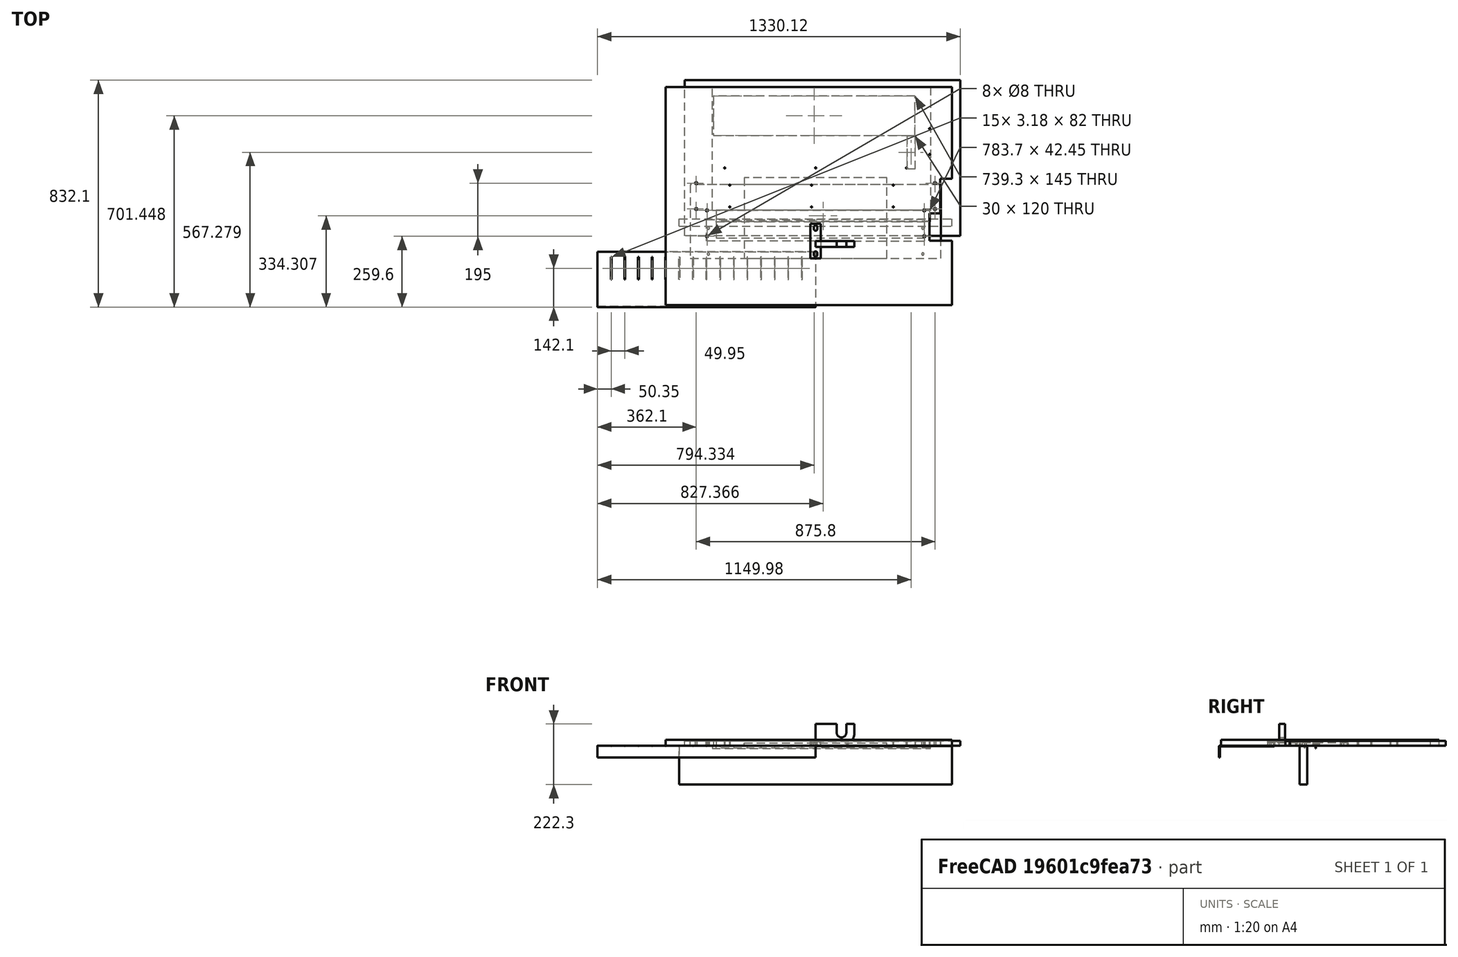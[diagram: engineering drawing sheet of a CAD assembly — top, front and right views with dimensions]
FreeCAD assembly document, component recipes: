
FREECAD ASSEMBLY — COMPONENT RECIPES ("cutting3")

This assembly document has 11 components, labeled P0..P10 below (a component is one placed body or linked part). 11 of them carry a construction recipe — the FreeCAD feature program that regenerates the part from scratch, quoted from this document or its linked companion documents; the rest are supplied as boundary geometry only. No exploded tour is included for this assembly.
COMPONENT P0 — recipe-attached ("filler_21", modeled in this document).
Construction recipe (the document's own serialized feature program — sketch geometry with constraints, then the solid features built on it; lengths are millimeters unless a unit is written):

FEATURE [Sketcher::SketchObject] Sketch006
  AttachmentSupport = -> [XY_Plane006]
  FullyConstrained = false
  MapMode = 5
  sketch-geometry (9):
    g0: LineSegment StartX=0 StartY=0 StartZ=0 EndX=19 EndY=0 EndZ=0
    g1: LineSegment StartX=19 StartY=0 StartZ=0 EndX=19 EndY=63.5 EndZ=0
    g2: LineSegment StartX=19 StartY=63.5 StartZ=0 EndX=0 EndY=63.5 EndZ=0
    g3: LineSegment StartX=0 StartY=63.5 StartZ=0 EndX=0 EndY=57 EndZ=0
    g4: ArcOfCircle CenterX=0 CenterY=44.5 CenterZ=0 NormalX=0 NormalY=0 NormalZ=1 AngleXU=0 Radius=6.5 StartAngle=4.7122 EndAngle=6.28319
    g5: ArcOfCircle CenterX=0 CenterY=50.5 CenterZ=0 NormalX=0 NormalY=0 NormalZ=1 AngleXU=0 Radius=6.5 StartAngle=3.65e-14 EndAngle=1.5708
    g6: LineSegment StartX=6.5 StartY=44.5 StartZ=0 EndX=6.5 EndY=50.5 EndZ=0
    g7: LineSegment StartX=-0.00123483 StartY=38 StartZ=0 EndX=0 EndY=0 EndZ=0
    g8: GeomPoint X=0 Y=47.5 Z=0
  constraints (23):
    c: Coincident(g0,g1)
    c: Coincident(g1,g2)
    c: Coincident(g2,g3)
    c: Coincident(g7,g0)
    c: Horizontal(g0)
    c: Horizontal(g2)
    c: Vertical(g1)
    c: Vertical(g3)
    c: Coincident(g0,g-1)
    c: DistanceX(g1) = 19
    c: DistanceY(g1) = 63.5
    c: Tangent(g4,g6) = -1.5708
    c: Tangent(g6,g5) = -1.5708
    c: Equal(g4,g5)
    c: PointOnObject(g4,g3)
    c: PointOnObject(g5,g3)
    c: Coincident(g3,g5)
    c: Coincident(g7,g4)
    c: DistanceY(g4,g3) = 19
    c: Diameter(g4) = 13
    c: PointOnObject(g8,g-2)
    c: Symmetric(g4,g5,g8)
    c: DistanceY(g8) = 47.5
FEATURE [PartDesign::Pad] Pad006
  Direction = (0,0,1)
  Length = 21
  Length2 = 10
  Profile = -> Sketch006
  ReferenceAxis = -> Sketch006 [N_Axis]
  Suppressed = false
  Type = 0
FEATURE [PartDesign::Mirrored] Mirrored002
  MirrorPlane = -> Sketch006 [V_Axis]
  Suppressed = false
FEATURE [PartDesign::Mirrored] Mirrored003
  MirrorPlane = -> Sketch006 [H_Axis]
  Suppressed = false
FEATURE [PartDesign::MultiTransform] MultiTransform
  BaseFeature = -> Pad006
  Originals = -> [Pad006]
  Suppressed = false
  Transformations = -> [Mirrored002,Mirrored003]
FEATURE [PartDesign::Body] Body002  label="filler_21"
  Group = -> [Sketch006,Pad006,MultiTransform,Mirrored002,Mirrored003]
  Origin = -> Origin006
  Tip = -> MultiTransform
COMPONENT P1 — recipe-attached ("filler_14.6", modeled in this document).
Construction recipe (the document's own serialized feature program — sketch geometry with constraints, then the solid features built on it; lengths are millimeters unless a unit is written):

FEATURE [Sketcher::SketchObject] Sketch007
  AttachmentSupport = -> [XY_Plane008]
  FullyConstrained = false
  MapMode = 5
  sketch-geometry (9):
    g0: LineSegment StartX=0 StartY=0 StartZ=0 EndX=19 EndY=0 EndZ=0
    g1: LineSegment StartX=19 StartY=0 StartZ=0 EndX=19 EndY=63.5 EndZ=0
    g2: LineSegment StartX=19 StartY=63.5 StartZ=0 EndX=0 EndY=63.5 EndZ=0
    g3: LineSegment StartX=0 StartY=63.5 StartZ=0 EndX=0 EndY=57 EndZ=0
    g4: ArcOfCircle CenterX=0 CenterY=44.5 CenterZ=0 NormalX=0 NormalY=0 NormalZ=1 AngleXU=0 Radius=6.5 StartAngle=4.7122 EndAngle=6.28319
    g5: ArcOfCircle CenterX=0 CenterY=50.5 CenterZ=0 NormalX=0 NormalY=0 NormalZ=1 AngleXU=0 Radius=6.5 StartAngle=3.65e-14 EndAngle=1.5708
    g6: LineSegment StartX=6.5 StartY=44.5 StartZ=0 EndX=6.5 EndY=50.5 EndZ=0
    g7: LineSegment StartX=-0.00123483 StartY=38 StartZ=0 EndX=0 EndY=0 EndZ=0
    g8: GeomPoint X=0 Y=47.5 Z=0
  constraints (23):
    c: Coincident(g0,g1)
    c: Coincident(g1,g2)
    c: Coincident(g2,g3)
    c: Coincident(g7,g0)
    c: Horizontal(g0)
    c: Horizontal(g2)
    c: Vertical(g1)
    c: Vertical(g3)
    c: Coincident(g0,g-1)
    c: DistanceX(g1) = 19
    c: DistanceY(g1) = 63.5
    c: Tangent(g4,g6) = -1.5708
    c: Tangent(g6,g5) = -1.5708
    c: Equal(g4,g5)
    c: PointOnObject(g4,g3)
    c: PointOnObject(g5,g3)
    c: Coincident(g3,g5)
    c: Coincident(g7,g4)
    c: DistanceY(g4,g3) = 19
    c: Diameter(g4) = 13
    c: PointOnObject(g8,g-2)
    c: Symmetric(g4,g5,g8)
    c: DistanceY(g8) = 47.5
FEATURE [PartDesign::Mirrored] Mirrored004
  MirrorPlane = -> Sketch007 [V_Axis]
  Suppressed = false
FEATURE [PartDesign::Mirrored] Mirrored005
  MirrorPlane = -> Sketch007 [H_Axis]
  Suppressed = false
FEATURE [PartDesign::Pad] Pad007
  Direction = (0,0,1)
  Length = 14.6
  Length2 = 10
  Profile = -> Sketch007
  ReferenceAxis = -> Sketch007 [N_Axis]
  Suppressed = false
  Type = 0
FEATURE [PartDesign::MultiTransform] MultiTransform001
  BaseFeature = -> Pad007
  Originals = -> [Pad007]
  Suppressed = false
  Transformations = -> [Mirrored004,Mirrored005]
FEATURE [PartDesign::Body] Body004  label="filler_14.6"
  Group = -> [Sketch007,Pad007,MultiTransform001,Mirrored004,Mirrored005]
  Origin = -> Origin008
  Tip = -> MultiTransform001
COMPONENT P2 — recipe-attached ("table1_ss", modeled in this document).
Construction recipe (the document's own serialized feature program — sketch geometry with constraints, then the solid features built on it; lengths are millimeters unless a unit is written):

FEATURE [PartDesign::SubShapeBinder] Binder002
  BindCopyOnChange = 0
  BindMode = 0
  ClaimChildren = false
  Context = -> Body009 [Binder002.]
  Fuse = false
  MakeFace = true
  OffsetFill = false
  OffsetIntersection = false
  OffsetJoinType = 0
  OffsetOpenResult = false
  PartialLoad = false
  Relative = true
  Support = -> [Body010[Sketch016.]]
  _Version = 2
FEATURE [Sketcher::SketchObject] Sketch010
  AttachmentSupport = -> [XY_Plane010]
  ExternalGeometry = -> [Binder002]
  FullyConstrained = false
  MapMode = 5
  sketch-geometry (4):
    g0: LineSegment StartX=-378.908 StartY=113.432 StartZ=0 EndX=-378.908 EndY=565.012 EndZ=0
    g1: LineSegment StartX=-378.908 StartY=565.012 StartZ=0 EndX=421.092 EndY=565.012 EndZ=0
    g2: LineSegment StartX=421.092 StartY=565.012 StartZ=0 EndX=421.092 EndY=113.432 EndZ=0
    g3: LineSegment StartX=421.092 StartY=113.432 StartZ=0 EndX=-378.908 EndY=113.432 EndZ=0
  constraints (10):
    c: Coincident(g0,g1)
    c: Coincident(g1,g2)
    c: Horizontal(g1)
    c: Vertical(g0)
    c: Vertical(g2)
    c: Coincident(g3,g2)
    c: PointOnObject(g2,g-3)
    c: Coincident(g3,g0)
    c: PointOnObject(g0,g-3)
    c: DistanceX(g3,g3) = 800
FEATURE [PartDesign::FeaturePython] BaseBend001  # WARN: FeaturePython — macro-defined, semantics opaque (R4)
  BendSide = 0
  BendSketch = -> Sketch010
  MidPlane = false
  Reverse = false
  Suppressed = false
  length = 100
  radius = 1
  thickness = 1
FEATURE [PartDesign::FeaturePython] Bend001  # WARN: FeaturePython — macro-defined, semantics opaque (R4)
  AutoMiter = true
  BaseFeature = -> BaseBend001
  BendType = 2
  LengthList = [10]
  LengthSpec = 0
  ReliefFactor = 0.7
  Suppressed = false
  UseReliefFactor = false
  angle = 90
  baseObject = -> BaseBend001 [Edge12]
  bendAList = [90]
  extend1 = 0
  extend2 = 0
  gap1 = 0
  gap2 = 0
  invert = false
  kfactor = 0.5
  length = 10
  maxExtendDist = 5
  minGap = 0.1
  minReliefGap = 1
  miterangle1 = 0
  miterangle2 = 0
  offset = 0
  radius = 1
  reliefType = 0
  reliefd = 1
  reliefw = 0.8
  sketchflip = false
  sketchinvert = false
  unfold = false
  expr: radius = BaseBend001.radius
FEATURE [PartDesign::SubShapeBinder] Binder
  BindCopyOnChange = 0
  BindMode = 0
  ClaimChildren = true
  Context = -> Body009 [Binder.]
  Fuse = false
  MakeFace = true
  OffsetFill = false
  OffsetIntersection = false
  OffsetJoinType = 0
  OffsetOpenResult = false
  PartialLoad = false
  Placement = pos=(-337,460,0) rot=(0,0,1;0rad)
  Relative = true
  Support = -> [Populate]
  _Version = 2
FEATURE [PartDesign::Body] Body009  label="table1_ss"
  Group = -> [Sketch010,Binder,BaseBend001,Binder002,Bend001]
  Origin = -> Origin010
  Tip = -> Bend001
COMPONENT P3 — recipe-attached ("table_plywood", modeled in this document).
Construction recipe (the document's own serialized feature program — sketch geometry with constraints, then the solid features built on it; lengths are millimeters unless a unit is written):

FEATURE [Sketcher::SketchObject] Sketch012
  AttachmentSupport = -> [XY_Plane011]
  FullyConstrained = false
  MapMode = 5
  sketch-geometry (4):
    g0: LineSegment StartX=-479.883 StartY=590 StartZ=0 EndX=530.117 EndY=590 EndZ=0
    g1: LineSegment StartX=530.117 StartY=590 StartZ=0 EndX=530.117 EndY=18.4008 EndZ=0
    g2: LineSegment StartX=530.117 StartY=18.4008 StartZ=0 EndX=-479.883 EndY=18.4008 EndZ=0
    g3: LineSegment StartX=-479.883 StartY=18.4008 StartZ=0 EndX=-479.883 EndY=590 EndZ=0
  constraints (10):
    c: Coincident(g0,g1)
    c: Coincident(g1,g2)
    c: Coincident(g2,g3)
    c: Coincident(g3,g0)
    c: Horizontal(g0)
    c: Horizontal(g2)
    c: Vertical(g1)
    c: Vertical(g3)
    c: DistanceX(g2,g2) = 1010
    c: DistanceY(g0) = 590
FEATURE [Sketcher::SketchObject] Sketch013
  AttachmentSupport = -> [XY_Plane011]
  FullyConstrained = false
  MapMode = 5
  expr: Constraints[8] = Sketch011.Constraints.width + LinearArray.SpanEnd
  expr: Constraints[9] = Sketch011.Constraints.length
  sketch-geometry (4):
    g0: LineSegment StartX=-375.316 StartY=386.848 StartZ=0 EndX=363.984 EndY=386.848 EndZ=0
    g1: LineSegment StartX=363.984 StartY=386.848 StartZ=0 EndX=363.984 EndY=531.848 EndZ=0
    g2: LineSegment StartX=363.984 StartY=531.848 StartZ=0 EndX=-375.316 EndY=531.848 EndZ=0
    g3: LineSegment StartX=-375.316 StartY=531.848 StartZ=0 EndX=-375.316 EndY=386.848 EndZ=0
  constraints (10):
    c: Coincident(g0,g1)
    c: Coincident(g1,g2)
    c: Coincident(g2,g3)
    c: Coincident(g3,g0)
    c: Horizontal(g0)
    c: Horizontal(g2)
    c: Vertical(g1)
    c: Vertical(g3)
    c: DistanceX(g2,g2) = 739.3
    c: DistanceY(g1,g1) = 145
FEATURE [Sketcher::SketchObject] Sketch014
  AttachmentSupport = -> [XY_Plane011]
  FullyConstrained = false
  MapMode = 5
  sketch-geometry (4):
    g0: LineSegment StartX=334.976 StartY=265.179 StartZ=0 EndX=364.976 EndY=265.179 EndZ=0
    g1: LineSegment StartX=364.976 StartY=265.179 StartZ=0 EndX=364.976 EndY=385.179 EndZ=0
    g2: LineSegment StartX=364.976 StartY=385.179 StartZ=0 EndX=334.976 EndY=385.179 EndZ=0
    g3: LineSegment StartX=334.976 StartY=385.179 StartZ=0 EndX=334.976 EndY=265.179 EndZ=0
  constraints (10):
    c: Coincident(g0,g1)
    c: Coincident(g1,g2)
    c: Coincident(g2,g3)
    c: Coincident(g3,g0)
    c: Horizontal(g0)
    c: Horizontal(g2)
    c: Vertical(g1)
    c: Vertical(g3)
    c: DistanceY(g3,g3) = 120
    c: DistanceX(g0,g0) = 30
FEATURE [Sketcher::SketchObject] Sketch016
  AttachmentSupport = -> [XY_Plane011]
  FullyConstrained = false
  MapMode = 5
  sketch-geometry (4):
    g0: LineSegment StartX=-364.484 StartY=70.9815 StartZ=0 EndX=419.215 EndY=70.9815 EndZ=0
    g1: LineSegment StartX=419.215 StartY=70.9815 StartZ=0 EndX=419.215 EndY=113.432 EndZ=0
    g2: LineSegment StartX=419.215 StartY=113.432 StartZ=0 EndX=-364.484 EndY=113.432 EndZ=0
    g3: LineSegment StartX=-364.484 StartY=113.432 StartZ=0 EndX=-364.484 EndY=70.9815 EndZ=0
  constraints (8):
    c: Coincident(g0,g1)
    c: Coincident(g1,g2)
    c: Coincident(g2,g3)
    c: Coincident(g3,g0)
    c: Horizontal(g0)
    c: Horizontal(g2)
    c: Vertical(g1)
    c: Vertical(g3)
FEATURE [PartDesign::Pad] Pad009
  Direction = (0,0,1)
  Length = 18
  Length2 = 10
  Profile = -> Sketch012
  ReferenceAxis = -> Sketch012 [N_Axis]
  Suppressed = false
  Type = 0
FEATURE [PartDesign::SubShapeBinder] Binder003
  BindCopyOnChange = 0
  BindMode = 0
  ClaimChildren = true
  Context = -> Body010 [Binder003.]
  Fuse = false
  MakeFace = true
  OffsetFill = false
  OffsetIntersection = false
  OffsetJoinType = 0
  OffsetOpenResult = false
  PartialLoad = false
  Relative = true
  Support = -> [Sketch014,Sketch013,Sketch016]
  _Version = 2
FEATURE [PartDesign::Pocket] Pocket002
  BaseFeature = -> Pad009
  Direction = (0,0,-1)
  Length = 5
  Length2 = 5
  Midplane = true
  Profile = -> Binder003
  Suppressed = false
  Type = 1
FEATURE [PartDesign::Body] Body010  label="table_plywood"
  Group = -> [Sketch012,Sketch013,Sketch014,Sketch016,Pad009,Binder003,Pocket002]
  Origin = -> Origin011
  Tip = -> Pocket002
COMPONENT P4 — recipe-attached ("table2_ss", modeled in this document).
Construction recipe (the document's own serialized feature program — sketch geometry with constraints, then the solid features built on it; lengths are millimeters unless a unit is written):

FEATURE [PartDesign::SubShapeBinder] Binder001
  BindCopyOnChange = 0
  BindMode = 0
  ClaimChildren = false
  Context = -> Body011 [Binder001.]
  Fuse = false
  MakeFace = true
  OffsetFill = false
  OffsetIntersection = false
  OffsetJoinType = 0
  OffsetOpenResult = false
  PartialLoad = false
  Relative = false
  Support = -> [Body010[Sketch016.]]
  _Version = 2
FEATURE [Sketcher::SketchObject] Sketch015
  AttachmentSupport = -> [XY_Plane012]
  ExternalGeometry = -> [Binder001]
  FullyConstrained = false
  MapMode = 5
  sketch-geometry (5):
    g0: LineSegment StartX=-364.484 StartY=11.9803 StartZ=0 EndX=419.215 EndY=11.9803 EndZ=0
    g1: LineSegment StartX=419.215 StartY=11.9803 StartZ=0 EndX=419.215 EndY=70.9815 EndZ=0
    g2: LineSegment StartX=419.215 StartY=70.9815 StartZ=0 EndX=-364.484 EndY=70.9815 EndZ=0
    g3: LineSegment StartX=-364.484 StartY=70.9815 StartZ=0 EndX=-364.484 EndY=11.9803 EndZ=0
    g4: GeomPoint X=27.3655 Y=41.4809 Z=0
  constraints (10):
    c: Coincident(g0,g1)
    c: Coincident(g1,g2)
    c: Coincident(g2,g3)
    c: Coincident(g3,g0)
    c: Horizontal(g0)
    c: Vertical(g1)
    c: Vertical(g3)
    c: Symmetric(g0,g1,g4)
    c: Coincident(g1,g-3)
    c: Coincident(g2,g-3)
FEATURE [PartDesign::FeaturePython] BaseBend  # WARN: FeaturePython — macro-defined, semantics opaque (R4)
  BendSide = 0
  BendSketch = -> Sketch015
  MidPlane = false
  Reverse = false
  Suppressed = false
  length = 100
  radius = 1
  thickness = 1
FEATURE [PartDesign::FeaturePython] Bend  # WARN: FeaturePython — macro-defined, semantics opaque (R4)
  AutoMiter = true
  BaseFeature = -> BaseBend
  BendType = 2
  LengthList = [10]
  LengthSpec = 1
  ReliefFactor = 0.7
  Suppressed = false
  UseReliefFactor = false
  angle = 90
  baseObject = -> BaseBend [Edge10]
  bendAList = [90]
  extend1 = 0
  extend2 = 0
  gap1 = 0
  gap2 = 0
  invert = false
  kfactor = 0.5
  length = 10
  maxExtendDist = 5
  minGap = 0.1
  minReliefGap = 1
  miterangle1 = 0
  miterangle2 = 0
  offset = 0
  radius = 1
  reliefType = 0
  reliefd = 1
  reliefw = 0.8
  sketchflip = false
  sketchinvert = false
  unfold = false
  expr: radius = BaseBend.radius
FEATURE [PartDesign::Body] Body011  label="table2_ss"
  Group = -> [Sketch015,BaseBend,Bend,Binder001]
  Origin = -> Origin012
  Tip = -> Bend
COMPONENT P5 — recipe-attached ("Body_2", modeled in this document).
Construction recipe (the document's own serialized feature program — sketch geometry with constraints, then the solid features built on it; lengths are millimeters unless a unit is written):

FEATURE [PartDesign::CoordinateSystem] LCS_0004
  AttacherType = Attacher::AttachEngine3D
  AttachmentSupport = -> [X_Axis010]
  MapMode = 2
FEATURE [Sketcher::SketchObject] Sketch009
  AttachmentSupport = -> [XY_Plane009]
  FullyConstrained = true
  MapMode = 5
  expr: Constraints[13] = <<P201003>>.Placement.Base.x
  expr: Constraints[15] = <<P201004>>.Placement.Base.x
  expr: Constraints[21] = P201_Bearing#Sketch.Constraints.total_width / 2
  expr: Constraints[3] = P201_Bearing#Sketch.Constraints.slot_d
  sketch-geometry (10):
    g0: Circle CenterX=393.3 CenterY=47.5 CenterZ=0 NormalX=0 NormalY=0 NormalZ=1 AngleXU=0 Radius=4.25
    g1: LineSegment StartX=460 StartY=-63.5 StartZ=0 EndX=460 EndY=206.5 EndZ=0
    g2: Circle CenterX=393.3 CenterY=-47.5 CenterZ=0 NormalX=0 NormalY=0 NormalZ=1 AngleXU=0 Radius=4.25
    g3: LineSegment StartX=-460 StartY=206.5 StartZ=0 EndX=-460 EndY=-63.5 EndZ=0
    g4: LineSegment StartX=-460 StartY=-63.5 StartZ=0 EndX=460 EndY=-63.5 EndZ=0
    g5: Circle CenterX=-393.3 CenterY=-47.5 CenterZ=0 NormalX=0 NormalY=0 NormalZ=1 AngleXU=0 Radius=4.25
    g6: Circle CenterX=-393.3 CenterY=47.5 CenterZ=0 NormalX=0 NormalY=0 NormalZ=1 AngleXU=0 Radius=4.25
    g7: GeomPoint X=393.3 Y=0 Z=0
    g8: LineSegment StartX=460 StartY=206.5 StartZ=0 EndX=0 EndY=206.5 EndZ=0
    g9: LineSegment StartX=0 StartY=206.5 StartZ=0 EndX=-460 EndY=206.5 EndZ=0
  constraints (28):
    c: Vertical(g1)
    c: Equal(g2,g0)
    c: Vertical(g2,g0)
    c: DistanceY(g2,g0) = 95
    c: Diameter(g2) = 8.5
    c: Coincident(g1,g8)
    c: Coincident(g9,g3)
    c: Vertical(g3)
    c: Coincident(g3,g4)
    c: Coincident(g4,g1)
    c: Horizontal(g4)
    c: Distance(g4) = 920
    c: Distance(g1) = 270
    c: DistanceX(g0) = 393.3
    c: Vertical(g6,g5)
    c: DistanceX(g6) = -393.3
    c: Equal(g2,g5)
    c: Equal(g5,g6)
    c: Horizontal(g6,g0)
    c: Horizontal(g2,g5)
    c: Symmetric(g2,g0,g7)
    c: DistanceY(g1,g7) = 63.5
    c: Horizontal(g7,g-1)
    c: Coincident(g8,g9)
    c: Horizontal(g8)
    c: Horizontal(g9)
    c: PointOnObject(g8,g-2)
    c: Equal(g9,g8)
FEATURE [PartDesign::Pad] Pad008
  Direction = (0,0,1)
  Length = 18
  Length2 = 10
  Profile = -> Sketch009
  ReferenceAxis = -> Sketch009 [N_Axis]
  Suppressed = false
  Type = 0
FEATURE [PartDesign::Body] Body_2
  Group = -> [LCS_0004,Sketch009,Pad008]
  Origin = -> Origin009
  Tip = -> Pad008
COMPONENT P6 — recipe-attached ("Model", modeled in this document).
Construction recipe (the document's own serialized feature program — sketch geometry with constraints, then the solid features built on it; lengths are millimeters unless a unit is written):

FEATURE [Sketcher::SketchObject] Sketch
  AttachmentSupport = -> [YZ_Plane001]
  FullyConstrained = false
  MapMode = 5
  Placement = pos=(0,0,0) rot=(0.57735,0.57735,0.57735;2.0944rad)
  sketch-geometry (4):
    g0: LineSegment StartX=0 StartY=0 StartZ=0 EndX=27.0682 EndY=0 EndZ=0
    g1: LineSegment StartX=27.0682 StartY=0 StartZ=0 EndX=27.0682 EndY=141.381 EndZ=0
    g2: LineSegment StartX=27.0682 StartY=141.381 StartZ=0 EndX=0 EndY=141.381 EndZ=0
    g3: LineSegment StartX=0 StartY=141.381 StartZ=0 EndX=0 EndY=0 EndZ=0
  constraints (9):
    c: Coincident(g0,g1)
    c: Coincident(g1,g2)
    c: Coincident(g2,g3)
    c: Coincident(g3,g0)
    c: Horizontal(g0)
    c: Horizontal(g2)
    c: Vertical(g1)
    c: Vertical(g3)
    c: Coincident(g0,g-1)
FEATURE [PartDesign::Pad] Pad
  Direction = (1,-2e-16,3e-16)
  Length = 1000
  Length2 = 10
  Midplane = true
  Placement = pos=(0,0,0) rot=(0.57735,0.57735,0.57735;2.0944rad)
  Profile = -> Sketch
  ReferenceAxis = -> Sketch [N_Axis]
  Suppressed = false
  Type = 0
FEATURE [PartDesign::Body] Body
  Group = -> [Sketch,Pad]
  Origin = -> Origin001
  Placement = pos=(0,54,-143) rot=(0,0,1;0rad)
  Tip = -> Pad
COMPONENT P7 — recipe-attached ("plywood_cutting_roll_support", modeled in this document).
Construction recipe (the document's own serialized feature program — sketch geometry with constraints, then the solid features built on it; lengths are millimeters unless a unit is written):

FEATURE [PartDesign::CoordinateSystem] LCS_0
  AttacherType = Attacher::AttachEngine3D
  AttachmentSupport = -> [X_Axis003]
  MapMode = 2
FEATURE [Sketcher::SketchObject] Sketch_1  label="basement_sketch"
  AttachmentSupport = -> [XY_Plane002]
  FullyConstrained = true
  MapMode = 5
  sketch-geometry (5):
    g0: LineSegment StartX=-500 StartY=-500 StartZ=0 EndX=550 EndY=-500 EndZ=0
    g1: LineSegment StartX=550 StartY=-500 StartZ=0 EndX=550 EndY=300 EndZ=0
    g2: LineSegment StartX=550 StartY=300 StartZ=0 EndX=-500 EndY=300 EndZ=0
    g3: LineSegment StartX=-500 StartY=300 StartZ=0 EndX=-500 EndY=-500 EndZ=0
    g4: GeomPoint X=-500 Y=-500 Z=0
  constraints (14):
    c: Coincident(g0,g1)
    c: Coincident(g1,g2)
    c: Coincident(g2,g3)
    c: Coincident(g3,g0)
    c: Horizontal(g0)
    c: Horizontal(g2)
    c: Vertical(g1)
    c: Vertical(g3)
    c: DistanceX(g0) = 550
    c: DistanceX(g4,g0) = 1050  'width'
    c: DistanceY(g0) = -500
    c: Distance(g1) = 800
    c: Distance(g-1,g3) = 500
    c: Coincident(g4,g0)
FEATURE [PartDesign::Pad] Pad001  label="basement_pad"
  Direction = (0,0,1)
  Length = 21
  Length2 = 10
  Profile = -> Sketch_1
  ReferenceAxis = -> Sketch_1 [N_Axis]
  Suppressed = false
  Type = 0
FEATURE [PartDesign::CoordinateSystem] top
  AttacherType = Attacher::AttachEngine3D
  AttachmentOffset = pos=(0,0,21) rot=(0,0,1;0rad)
  AttachmentSupport = -> [XY_Plane002]
  MapMode = 5
  Placement = pos=(0,0,21) rot=(0,0,1;0rad)
  expr: .AttachmentOffset.Base.z = Pad001.Length
FEATURE [Sketcher::SketchObject] Sketch003
  AttachmentSupport = -> [XY_Plane002]
  FullyConstrained = true
  MapMode = 5
  expr: Constraints[15] = P204.Placement.Base.x
  expr: Constraints[16] = P204001.Placement.Base.x
  expr: Constraints[24] = P201001.Placement.Base.x
  expr: Constraints[2] = P201.Placement.Base.x
  expr: Constraints[49] = roll_75x710.Placement.Base.y - cutting_roll.Placement.Base.y
  expr: Constraints[59] = <<top_opening_axis_pearing>>.Placement.Base.x
  expr: Constraints[60] = <<top_opening_axis_pearing>>.Placement.Base.y
  sketch-geometry (27):
    g0: Circle CenterX=-398.3 CenterY=-47.5 CenterZ=0 NormalX=0 NormalY=0 NormalZ=1 AngleXU=0 Radius=4
    g1: Circle CenterX=-398.3 CenterY=47.5 CenterZ=0 NormalX=0 NormalY=0 NormalZ=1 AngleXU=0 Radius=4
    g2: Circle CenterX=398.3 CenterY=-47.5 CenterZ=0 NormalX=0 NormalY=0 NormalZ=1 AngleXU=0 Radius=4
    g3: Circle CenterX=398.3 CenterY=47.5 CenterZ=0 NormalX=0 NormalY=0 NormalZ=1 AngleXU=0 Radius=4
    g4: Circle CenterX=-437.9 CenterY=-147.5 CenterZ=0 NormalX=0 NormalY=0 NormalZ=1 AngleXU=0 Radius=4
    g5: Circle CenterX=-437.9 CenterY=-52.5 CenterZ=0 NormalX=0 NormalY=0 NormalZ=1 AngleXU=0 Radius=4
    g6: Circle CenterX=437.9 CenterY=-147.5 CenterZ=0 NormalX=0 NormalY=0 NormalZ=1 AngleXU=0 Radius=4
    g7: Circle CenterX=437.9 CenterY=-52.5 CenterZ=0 NormalX=0 NormalY=0 NormalZ=1 AngleXU=0 Radius=4
    g8: Circle CenterX=15 CenterY=-140 CenterZ=0 NormalX=0 NormalY=0 NormalZ=1 AngleXU=0 Radius=2
    g9: Circle CenterX=15 CenterY=-60 CenterZ=0 NormalX=0 NormalY=0 NormalZ=1 AngleXU=0 Radius=2
    g10: Circle CenterX=315 CenterY=-60 CenterZ=0 NormalX=0 NormalY=0 NormalZ=1 AngleXU=0 Radius=2
    g11: Circle CenterX=315 CenterY=-140 CenterZ=0 NormalX=0 NormalY=0 NormalZ=1 AngleXU=0 Radius=2
    g12: Circle CenterX=-285 CenterY=-140 CenterZ=0 NormalX=0 NormalY=0 NormalZ=1 AngleXU=0 Radius=2
    g13: Circle CenterX=-285 CenterY=-60 CenterZ=0 NormalX=0 NormalY=0 NormalZ=1 AngleXU=0 Radius=2
    g14: LineSegment StartX=-398.3 StartY=-47.5 StartZ=0 EndX=-398.3 EndY=0 EndZ=0
    g15: LineSegment StartX=-398.3 StartY=0 StartZ=0 EndX=-398.3 EndY=47.5 EndZ=0
    g16: LineSegment StartX=-437.9 StartY=-147.5 StartZ=0 EndX=-437.9 EndY=-100 EndZ=0
    g17: LineSegment StartX=-437.9 StartY=-100 StartZ=0 EndX=-437.9 EndY=-52.5 EndZ=0
    g18: LineSegment StartX=315 StartY=-140 StartZ=0 EndX=315 EndY=-100 EndZ=0
    g19: LineSegment StartX=315 StartY=-100 StartZ=0 EndX=315 EndY=-60 EndZ=0
    g20: Circle CenterX=-418 CenterY=-252.5 CenterZ=0 NormalX=0 NormalY=0 NormalZ=1 AngleXU=0 Radius=2
    g21: Circle CenterX=-418 CenterY=-347.5 CenterZ=0 NormalX=0 NormalY=0 NormalZ=1 AngleXU=0 Radius=2
    g22: LineSegment StartX=-418 StartY=-347.5 StartZ=0 EndX=-418 EndY=-300 EndZ=0
    g23: LineSegment StartX=-418 StartY=-300 StartZ=0 EndX=-418 EndY=-252.5 EndZ=0
    g24: Circle CenterX=0 CenterY=-203 CenterZ=0 NormalX=0 NormalY=0 NormalZ=1 AngleXU=0 Radius=2
    g25: Circle CenterX=333.333 CenterY=-203 CenterZ=0 NormalX=0 NormalY=0 NormalZ=1 AngleXU=0 Radius=2
    g26: Circle CenterX=-333.333 CenterY=-203 CenterZ=0 NormalX=0 NormalY=0 NormalZ=1 AngleXU=0 Radius=2
  constraints (74):
    c: Vertical(g0,g1)
    c: DistanceY(g0,g1) = 95
    c: DistanceX(g0) = -398.3
    c: Diameter(g0) = 8
    c: Equal(g2,g3)
    c: Equal(g3,g1)
    c: Equal(g1,g0)
    c: Vertical(g6,g7)
    c: Vertical(g5,g4)
    c: Horizontal(g4,g6)
    c: Horizontal(g7,g5)
    c: Equal(g4,g5)
    c: Equal(g5,g7)
    c: Equal(g7,g6)
    c: Equal(g6,g0)
    c: DistanceX(g4) = -437.9
    c: DistanceX(g6) = 437.9
    c: Coincident(g14,g0)
    c: Coincident(g15,g1)
    c: Coincident(g16,g4)
    c: Coincident(g17,g5)
    c: Vertical(g2,g3)
    c: Horizontal(g2,g0)
    c: Horizontal(g3,g1)
    c: DistanceX(g2) = 398.3
    c: Equal(g13,g9)
    c: Equal(g9,g10)
    c: Equal(g10,g12)
    c: Equal(g12,g8)
    c: Equal(g8,g11)
    c: Horizontal(g12,g8)
    c: Horizontal(g13,g9)
    c: Vertical(g11,g10)
    c: Diameter(g8) = 4
    c: Symmetric(g11,g12,g8)
    c: Symmetric(g13,g10,g9)
    c: Coincident(g14,g15)
    c: Coincident(g16,g17)
    c: Equal(g15,g14)
    c: Equal(g17,g16)
    c: Vertical(g14)
    c: Vertical(g16)
    c: Equal(g14,g16)
    c: Coincident(g18,g11)
    c: Vertical(g18)
    c: Coincident(g18,g19)
    c: Coincident(g19,g10)
    c: Equal(g18,g19)
    c: Horizontal(g18,g16)
    c: DistanceY(g7,g3) = 100
    c: Coincident(g22,g21)
    c: Vertical(g22)
    c: Coincident(g23,g22)
    c: Coincident(g23,g20)
    c: Vertical(g23)
    c: Equal(g22,g23)
    c: Equal(g21,g20)
    c: Equal(g23,g15)
    c: PointOnObject(g14,g-1)
    c: DistanceX(g22) = -418
    c: DistanceY(g22) = -300
    c: DistanceY(g12,g13) = 80
    c: Horizontal(g26,g25)
    c: Symmetric(g26,g25,g24)
    c: DistanceY(g24) = -203
    c: Equal(g26,g24)
    c: Equal(g24,g25)
    c: Equal(g25,g8)
    c: DistanceX(g25) = 333.333
    c: Equal(g20,g8)
    c: DistanceX(g8) = 15
    c: PointOnObject(g24,g-2)
    c: Vertical(g8,g9)
    c: DistanceX(g12,g8) = 300
FEATURE [PartDesign::Pocket] Pocket
  BaseFeature = -> Pad001
  Direction = (0,0,-1)
  Length = 5
  Length2 = 5
  Midplane = true
  Profile = -> Sketch003
  ReferenceAxis = -> Sketch003 [N_Axis]
  Suppressed = false
  Type = 1
FEATURE [PartDesign::CoordinateSystem] Local_CS  label="top_opening_axis_pearing"
  AttacherType = Attacher::AttachEngine3D
  AttachmentOffset = pos=(-418,-300,21) rot=(0,0,1;0rad)
  AttachmentSupport = -> [XY_Plane002]
  MapMode = 5
  Placement = pos=(-418,-300,21) rot=(0,0,1;0rad)
  expr: .AttachmentOffset.Base.z = Pad001.Length
FEATURE [Sketcher::SketchObject] Sketch008
  AttachmentSupport = -> [XY_Plane002]
  FullyConstrained = false
  MapMode = 5
  expr: Constraints[13] = <<P201_Bearing>>#Sketch.Constraints.total_width / 2
  expr: Constraints[14] = <<P201_Bearing>>#Sketch.Constraints.total_width
  sketch-geometry (6):
    g0: LineSegment StartX=-417.3 StartY=63.5 StartZ=0 EndX=-417.3 EndY=-36.4807 EndZ=0
    g1: LineSegment StartX=-417.3 StartY=-36.4807 StartZ=0 EndX=-456.873 EndY=-36.4807 EndZ=0
    g2: LineSegment StartX=-456.873 StartY=-36.4807 StartZ=0 EndX=-456.873 EndY=-163.481 EndZ=0
    g3: LineSegment StartX=-456.873 StartY=-163.481 StartZ=0 EndX=-754.283 EndY=-163.481 EndZ=0
    g4: LineSegment StartX=-754.283 StartY=-163.481 StartZ=0 EndX=-754.283 EndY=63.5 EndZ=0
    g5: LineSegment StartX=-754.283 StartY=63.5 StartZ=0 EndX=-417.3 EndY=63.5 EndZ=0
  constraints (15):
    c: Vertical(g0)
    c: Coincident(g0,g1)
    c: Horizontal(g1)
    c: Coincident(g1,g2)
    c: Vertical(g2)
    c: Coincident(g2,g3)
    c: Horizontal(g3)
    c: Coincident(g3,g4)
    c: Vertical(g4)
    c: Coincident(g4,g5)
    c: Coincident(g5,g0)
    c: Horizontal(g5)
    c: DistanceX(g0) = -417.3
    c: DistanceY(g0) = 63.5
    c: DistanceY(g2,g2) = 127
FEATURE [PartDesign::Pocket] Pocket001
  BaseFeature = -> Pocket
  Direction = (0,0,-1)
  Length = 5
  Length2 = 5
  Midplane = true
  Profile = -> Sketch008
  ReferenceAxis = -> Sketch008 [N_Axis]
  Suppressed = false
  Type = 1
FEATURE [PartDesign::Body] plywood_cutting_roll_support
  AssemblyType = Part::Link
  AttachedBy = #top
  AttachedTo = Parent Assembly#LCS_Origin
  AttachmentOffset = pos=(0,0,-82.3) rot=(0,0,1;0rad)
  Group = -> [LCS_0,Sketch_1,Pad001,top,Sketch003,Pocket,Local_CS,Sketch008,Pocket001]
  Origin = -> Origin002
  Placement = pos=(0,65,0) rot=(0,0,1;3.14159rad)
  SolverId = Asm4EE
  Tip = -> Pocket001
  expr: .AttachmentOffset.Base.z = -(<<roll_75x710mm>>#roll_75_sketch.Constraints.r * 2 + 7.3 mm + 21 mm - 14.3 mm)
COMPONENT P8 — recipe-attached ("plywood_top", modeled in this document).
Construction recipe (the document's own serialized feature program — sketch geometry with constraints, then the solid features built on it; lengths are millimeters unless a unit is written):

FEATURE [PartDesign::CoordinateSystem] LCS_0003
  AttacherType = Attacher::AttachEngine3D
  AttachmentSupport = -> [X_Axis006]
  MapMode = 2
FEATURE [Sketcher::SketchObject] Sketch004
  AttachmentSupport = -> [XY_Plane005]
  FullyConstrained = false
  MapMode = 5
  sketch-geometry (5):
    g0: LineSegment StartX=-261.681 StartY=232.193 StartZ=0 EndX=-261.681 EndY=-63.5 EndZ=0
    g1: LineSegment StartX=-261.681 StartY=-63.5 StartZ=0 EndX=261.681 EndY=-63.5 EndZ=0
    g2: LineSegment StartX=261.681 StartY=-63.5 StartZ=0 EndX=261.681 EndY=232.193 EndZ=0
    g3: LineSegment StartX=261.681 StartY=232.193 StartZ=0 EndX=-261.681 EndY=232.193 EndZ=0
    g4: GeomPoint X=0 Y=84.3466 Z=0
  constraints (11):
    c: Coincident(g0,g1)
    c: Coincident(g1,g2)
    c: Coincident(g2,g3)
    c: Coincident(g3,g0)
    c: Horizontal(g1)
    c: Horizontal(g3)
    c: Vertical(g0)
    c: Vertical(g2)
    c: Symmetric(g1,g0,g4)
    c: PointOnObject(g4,g-2)
    c: Distance(g-1,g1) = 63.5
FEATURE [PartDesign::Pad] Pad004
  Direction = (0,0,1)
  Length = 10
  Length2 = 10
  Profile = -> Sketch004
  ReferenceAxis = -> Sketch004 [N_Axis]
  Suppressed = false
  Type = 0
FEATURE [PartDesign::CoordinateSystem] Local_CS001  label="top001"
  AttacherType = Attacher::AttachEngine3D
  AttachmentOffset = pos=(0,0,10) rot=(0,0,1;0rad)
  AttachmentSupport = -> [XY_Plane005]
  MapMode = 5
  Placement = pos=(0,0,10) rot=(0,0,1;0rad)
  expr: .AttachmentOffset.Base.z = Pad004.Length
FEATURE [PartDesign::Body] plywood_top
  Group = -> [LCS_0003,Sketch004,Pad004,Local_CS001]
  Origin = -> Origin005
  Tip = -> Pad004
COMPONENT P9 — recipe-attached ("shield_fixture", modeled in this document).
Construction recipe (the document's own serialized feature program — sketch geometry with constraints, then the solid features built on it; lengths are millimeters unless a unit is written):

FEATURE [PartDesign::CoordinateSystem] LCS_0001
  AttacherType = Attacher::AttachEngine3D
  AttachmentSupport = -> [X_Axis004]
  MapMode = 2
FEATURE [Sketcher::SketchObject] Sketch005  label="shield_fixture_sketch"
  AttachmentSupport = -> [XY_Plane003]
  FullyConstrained = true
  MapMode = 5
  expr: .Constraints.length = abs(<<plywood_cutting_roll_support001>>.AttachmentOffset.Base.z) - <<plywood_cutting_shield>>#Pad.Length
  sketch-geometry (4):
    g0: LineSegment StartX=0 StartY=0 StartZ=0 EndX=400 EndY=0 EndZ=0
    g1: LineSegment StartX=400 StartY=0 StartZ=0 EndX=400 EndY=79.3 EndZ=0
    g2: LineSegment StartX=400 StartY=79.3 StartZ=0 EndX=0 EndY=79.3 EndZ=0
    g3: LineSegment StartX=0 StartY=79.3 StartZ=0 EndX=0 EndY=0 EndZ=0
  constraints (11):
    c: Coincident(g0,g1)
    c: Coincident(g1,g2)
    c: Coincident(g2,g3)
    c: Coincident(g3,g0)
    c: Horizontal(g0)
    c: Horizontal(g2)
    c: Vertical(g1)
    c: Vertical(g3)
    c: Coincident(g0,g-1)
    c: Distance(g3) = 79.3  'length'
    c: Distance(g0) = 400  'width'
FEATURE [PartDesign::Pad] Pad005  label="shield_fixture_pad"
  Direction = (0,0,1)
  Length = 16
  Length2 = 10
  Profile = -> Sketch005
  ReferenceAxis = -> Sketch005 [N_Axis]
  Suppressed = false
  Type = 0
FEATURE [PartDesign::Mirrored] Mirrored001
  BaseFeature = -> Pad005
  MirrorPlane = -> Sketch005 [V_Axis]
  Originals = -> [Pad005]
  Suppressed = false
FEATURE [PartDesign::Body] shield_fixture
  Group = -> [LCS_0001,Sketch005,Pad005,Mirrored001]
  Origin = -> Origin003
  Tip = -> Mirrored001
COMPONENT P10 — recipe-attached ("shield_fixture_lengthwise", modeled in this document).
Construction recipe (the document's own serialized feature program — sketch geometry with constraints, then the solid features built on it; lengths are millimeters unless a unit is written):

FEATURE [PartDesign::CoordinateSystem] LCS_0002
  AttacherType = Attacher::AttachEngine3D
  AttachmentSupport = -> [X_Axis005]
  MapMode = 2
FEATURE [Sketcher::SketchObject] Sketch002
  AttachmentSupport = -> [XZ_Plane004]
  FullyConstrained = true
  MapMode = 5
  Placement = pos=(0,0,0) rot=(1,0,0;1.5708rad)
  expr: .Constraints.height = <<shield_fixture_sketch>>.Constraints.length
  expr: Constraints[9] = -(-<<cutting_roll>>.Placement.Base.y + shield_fixture001.Placement.Base.y)
  sketch-geometry (10):
    g0: LineSegment StartX=0 StartY=0 StartZ=0 EndX=95 EndY=0 EndZ=0
    g1: LineSegment StartX=142.5 StartY=47.5 StartZ=0 EndX=142.5 EndY=79.3 EndZ=0
    g2: LineSegment StartX=112.5 StartY=79.3 StartZ=0 EndX=112.5 EndY=47.5 EndZ=0
    g3: LineSegment StartX=77.5 StartY=47.5 StartZ=0 EndX=77.5 EndY=79.3 EndZ=0
    g4: LineSegment StartX=0 StartY=79.3 StartZ=0 EndX=0 EndY=0 EndZ=0
    g5: ArcOfCircle CenterX=95 CenterY=47.5 CenterZ=0 NormalX=0 NormalY=0 NormalZ=1 AngleXU=0 Radius=17.5 StartAngle=3.14159 EndAngle=6.28319
    g6: LineSegment StartX=77.5 StartY=79.3 StartZ=0 EndX=0 EndY=79.3 EndZ=0
    g7: LineSegment StartX=112.5 StartY=79.3 StartZ=0 EndX=142.5 EndY=79.3 EndZ=0
    g8: ArcOfCircle CenterX=95 CenterY=47.5 CenterZ=0 NormalX=0 NormalY=0 NormalZ=1 AngleXU=0 Radius=47.5 StartAngle=4.71239 EndAngle=6.28319
    g9: GeomPoint X=142.5 Y=0 Z=0
  constraints (25):
    c: Coincident(g-1,g0)
    c: PointOnObject(g9,g-1)
    c: Vertical(g1)
    c: Vertical(g2)
    c: Vertical(g3)
    c: Coincident(g4,g0)
    c: Horizontal(g3,g2)
    c: Tangent(g5,g2) = 1.5708
    c: Tangent(g5,g3) = 1.5708
    c: DistanceX(g5) = 95
    c: Diameter(g5) = 35
    c: Coincident(g6,g3)
    c: PointOnObject(g6,g-2)
    c: Horizontal(g6)
    c: Coincident(g7,g2)
    c: Horizontal(g7)
    c: Coincident(g1,g7)
    c: Coincident(g4,g6)
    c: DistanceY(g4,g4) = 79.3  'height'
    c: DistanceY(g5) = 47.5
    c: PointOnObject(g9,g0)
    c: PointOnObject(g9,g1)
    c: Tangent(g0,g8) = -1.5708
    c: Tangent(g1,g8) = -1.5708
    c: Coincident(g8,g5)
FEATURE [PartDesign::Pad] Pad003
  Direction = (0,-1,2e-16)
  Length = 21
  Length2 = 10
  Placement = pos=(0,0,0) rot=(1,0,0;1.5708rad)
  Profile = -> Sketch002
  ReferenceAxis = -> Sketch002 [N_Axis]
  Suppressed = false
  Type = 0
FEATURE [PartDesign::Body] shield_fixture_lengthwise
  Group = -> [LCS_0002,Sketch002,Pad003]
  Origin = -> Origin004
  Tip = -> Pad003
PROVENANCE & LICENSES
A FreeCAD (.FCStd) document from a public repository crawl; recipes are the document's own serialized feature recipes (and, for linked parts, companion documents' recipes).
License: as declared in the source repository (recorded in the dataset sidecar).
